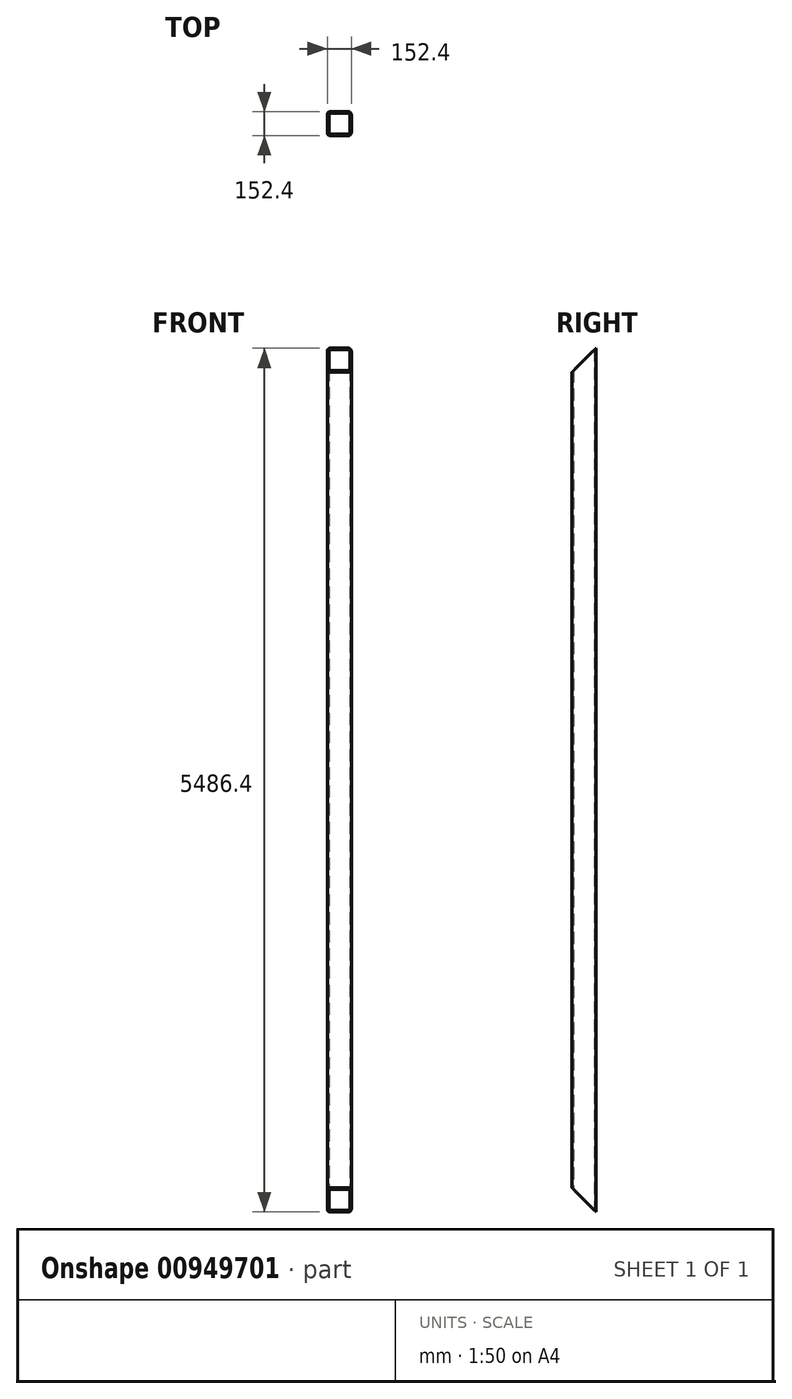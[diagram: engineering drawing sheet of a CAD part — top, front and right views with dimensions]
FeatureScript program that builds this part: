
annotation { "Feature Type Name" : "Feature", "Feature Type Description" : "" }
export const myFeature = defineFeature(function(context is Context, id is Id, definition is map)
    precondition{}
    {
        {
            var Q0;
            Q0=qCreatedBy(makeId("Top.planeOp"),FACE);
            var sketch = newSketch(context, id + "F0", { "sketchPlane" : qUnion([Q0])});
            skLineSegment(sketch, "E0.bottom", {"start": v(-57.15, -76.2) * mm, "end": v(57.15, -76.2) * mm});
            skLineSegment(sketch, "E0.top", {"start": v(-57.15, 76.2) * mm, "end": v(57.15, 76.2) * mm});
            skLineSegment(sketch, "E0.left", {"start": v(-76.2, -57.15) * mm, "end": v(-76.2, 57.15) * mm});
            skLineSegment(sketch, "E0.right", {"start": v(76.2, -57.15) * mm, "end": v(76.2, 57.15) * mm});
            skPoint(sketch, "E0.middle", {"position": v(0, 0) * mm});
            skLineSegment(sketch, "E1.bottom", {"start": v(-57.15, -66.68) * mm, "end": v(57.15, -66.68) * mm});
            skLineSegment(sketch, "E1.top", {"start": v(-57.15, 66.68) * mm, "end": v(57.15, 66.68) * mm});
            skLineSegment(sketch, "E1.left", {"start": v(-66.68, -57.15) * mm, "end": v(-66.68, 57.15) * mm});
            skLineSegment(sketch, "E1.right", {"start": v(66.68, -57.15) * mm, "end": v(66.68, 57.15) * mm});
            skPoint(sketch, "E2.visualSharp", {"position": v(-76.2, 76.2) * mm});
            skArc(sketch, "E2.filletArc", {"start": v(-57.15, 76.2) * mm, "mid": v(-70.62, 70.62) * mm, "end": v(-76.2, 57.15) * mm});
            skPoint(sketch, "E3.visualSharp", {"position": v(-76.2, -76.2) * mm});
            skArc(sketch, "E3.filletArc", {"start": v(-76.2, -57.15) * mm, "mid": v(-70.62, -70.62) * mm, "end": v(-57.15, -76.2) * mm});
            skPoint(sketch, "E4.visualSharp", {"position": v(76.2, -76.2) * mm});
            skArc(sketch, "E4.filletArc", {"start": v(57.15, -76.2) * mm, "mid": v(70.62, -70.62) * mm, "end": v(76.2, -57.15) * mm});
            skPoint(sketch, "E5.visualSharp", {"position": v(76.2, 76.2) * mm});
            skArc(sketch, "E5.filletArc", {"start": v(76.2, 57.15) * mm, "mid": v(70.62, 70.62) * mm, "end": v(57.15, 76.2) * mm});
            skPoint(sketch, "E6.visualSharp", {"position": v(-66.68, 66.68) * mm});
            skArc(sketch, "E6.filletArc", {"start": v(-57.15, 66.68) * mm, "mid": v(-63.89, 63.89) * mm, "end": v(-66.68, 57.15) * mm});
            skPoint(sketch, "E7.visualSharp", {"position": v(-66.68, -66.68) * mm});
            skArc(sketch, "E7.filletArc", {"start": v(-66.68, -57.15) * mm, "mid": v(-63.89, -63.89) * mm, "end": v(-57.15, -66.68) * mm});
            skPoint(sketch, "E8.visualSharp", {"position": v(66.68, -66.68) * mm});
            skArc(sketch, "E8.filletArc", {"start": v(57.15, -66.68) * mm, "mid": v(63.89, -63.89) * mm, "end": v(66.68, -57.15) * mm});
            skPoint(sketch, "E9.visualSharp", {"position": v(66.68, 66.68) * mm});
            skArc(sketch, "E9.filletArc", {"start": v(66.68, 57.15) * mm, "mid": v(63.89, 63.89) * mm, "end": v(57.15, 66.68) * mm});
            skSolve(sketch);
        }
        {
            var Q0;
            Q0=qSketchRegion(id+"F0",true);
            extrude(context, id + "F1", {"entities" : qUnion([Q0]), "depth" : 5486.4 * mm, "offsetDistance" : 25.4 * mm});
        }
        {
            var Q0;
            Q0=qCreatedBy(makeId("Right.planeOp"),FACE);
            var sketch = newSketch(context, id + "F2", { "sketchPlane" : qUnion([Q0])});
            skLineSegment(sketch, "E10", {"start": v(-76.2, 5486.4) * mm, "end": v(76.2, 5486.4) * mm});
            skLineSegment(sketch, "E11", {"start": v(76.2, 5486.4) * mm, "end": v(-76.2, 5334) * mm});
            skLineSegment(sketch, "E12", {"start": v(-76.2, 5334) * mm, "end": v(-76.2, 5486.4) * mm});
            skLineSegment(sketch, "E13", {"start": v(76.2, 0) * mm, "end": v(-76.2, 0) * mm});
            skLineSegment(sketch, "E14", {"start": v(-76.2, 0) * mm, "end": v(-76.2, 152.4) * mm});
            skLineSegment(sketch, "E15", {"start": v(-76.2, 152.4) * mm, "end": v(76.2, 0) * mm});
            skSolve(sketch);
        }
        {
            var Q0;
            Q0=qSketchRegion(id+"F2",true);
            extrude(context, id + "F3", {"entities" : qUnion([Q0]), "operationType" : NewBodyOperationType.REMOVE, "endBound" : BoundingType.THROUGH_ALL, "oppositeDirection" : true, "depth" : 25.4 * mm, "offsetDistance" : 25.4 * mm, "hasSecondDirection" : true, "secondDirectionBound" : SecondDirectionBoundingType.THROUGH_ALL, "secondDirectionOppositeDirection" : false, "secondDirectionDepth" : 25.4 * mm});
        }
    });
